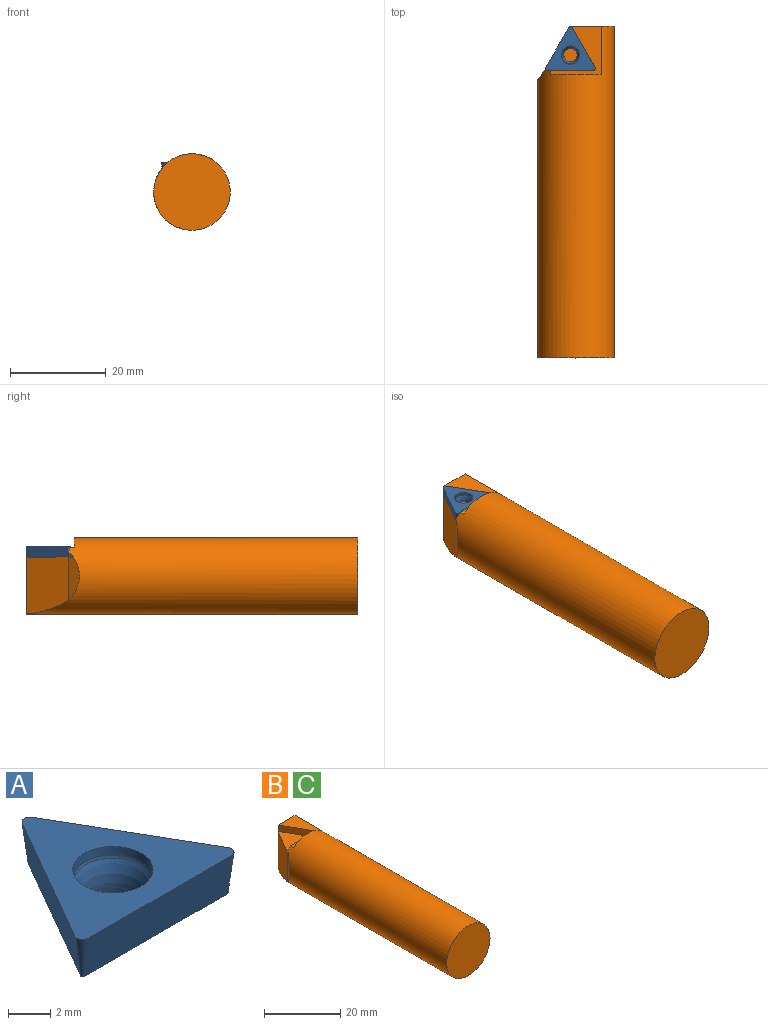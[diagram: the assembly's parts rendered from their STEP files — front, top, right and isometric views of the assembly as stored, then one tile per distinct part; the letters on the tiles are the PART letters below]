
ASSEMBLY  parts=3 mates=1
PART A: 16 faces, bbox 10.4x9.1x3.8 mm
  f0: plane 8.34x4.82mm, normal (0.86,0.5,-0.12), area 0.8mm2, adj f1,f5,f7,f12
  f1: plane 9.83x8.54mm, normal (0,0,-1), area 37mm2, adj f0,f2,f3,f5,f6,f7,f10
  f2: plane 8.48x5.07mm, normal (-0.86,0.5,-0.12), area 23.1mm2, adj f1,f4,f6,f7
  f3: plane 9.62x2.38mm, normal (0,-0.99,-0.12), area 23.1mm2, adj f1,f4,f5,f6
  f4: plane 10.42x9.13mm, normal (0,0,1), area 40.5mm2, adj f2,f3,f5,f6,f7,f8,f15
  f5: cone r=0.4mm half-angle=7deg, axis (0,0,1), area 1.3mm2, adj f0,f1,f3,f4,f14
  f6: cone r=0.4mm half-angle=7deg, axis (0,0,1), area 1.3mm2, adj f1,f2,f3,f4
  f7: cone r=0.4mm half-angle=7deg, axis (0,0,1), area 1.3mm2, adj f0,f1,f2,f4,f13
  f8: cone r=1.88mm half-angle=4deg, axis (0,0,1), area 5.7mm2, adj f4,f11
  f9: torus R=3.9mm, axis (0,0,1), area 14.4mm2, adj f10,f11
  f10: cylinder r=1.4mm len=2.8mm, axis (0,0,1), area 3.1mm2, adj f1,f9
  f11: torus R=1.58mm, axis (0,0,-1), area 1.8mm2, adj f8,f9
  f12: plane 8.48x5.06mm, normal (0,0,-1), area 2.7mm2, adj f0,f13,f14,f15
  f13: plane 2.3x0.24mm, normal (-0.5,0.87,0), area 0.3mm2, adj f7,f12,f15
  f14: plane 2.3x0.24mm, normal (0.5,-0.87,0), area 0.3mm2, adj f5,f12,f15
  f15: plane 8.33x4.81mm, normal (0.87,0.5,0), area 22.1mm2, adj f4,f12,f13,f14
PART B: 14 faces, bbox 16x69.4x16 mm
  f0: plane 0.09x0.07mm, normal (0,0,-1), area 0mm2, adj f5,f9,f13
  f1: plane 10.58x10.13mm, normal (0,0,1), area 45.6mm2, adj f2,f4,f5,f7,f10,f11
  f2: cylinder r=8mm len=69.43mm, axis (0,1,0), area 3218.5mm2, adj f1,f3,f4,f5,f8,f9,f10,f12
  f3: plane 16x16mm, normal (0,-1,0), area 201.1mm2, adj f2
  f4: plane 10.58x2mm, normal (0,1,0), area 14.5mm2, adj f1,f2
  f5: plane 10.49x2mm, normal (0,1,0), area 20.5mm2, adj f0,f1,f2,f6,f7,f13
  f6: plane 10.47x8.96mm, normal (0,0,1), area 46.9mm2, adj f5,f7,f8,f10,f11
  f7: plane 8.95x5.17mm, normal (-0.87,-0.5,0), area 20.7mm2, adj f1,f5,f6,f11
  f8: plane 11.94x8.96mm, normal (-0.86,0.51,0), area 113.4mm2, adj f2,f6,f9,f10
  f9: plane 8.93x2.24mm, normal (-0.8,0.61,0), area 18.4mm2, adj f0,f2,f8,f12
  f10: plane 14x9mm, normal (0,1,0), area 107.2mm2, adj f1,f2,f6,f8,f11
  f11: plane 2x0.01mm, normal (-0.86,0.51,0), area 0mm2, adj f1,f6,f7,f10
  f12: plane 0.94x0.56mm, normal (0,0,1), area 0.1mm2, adj f2,f9,f13
  f13: plane 1.03x0.91mm, normal (-0.86,0.51,0), area 0.6mm2, adj f0,f2,f5,f12
PART C: same geometry as B
PLACE A t=(-2.24,9.66,-21.39)mm
PLACE B t=(4.41,19.47,-27.54)mm
PLACE C t=(4.41,19.47,-27.54)mm
MATE parallel A.f15 <-> B.f7  axis (0.87,0.5,0) through (6,14.42,-22.54)mm
